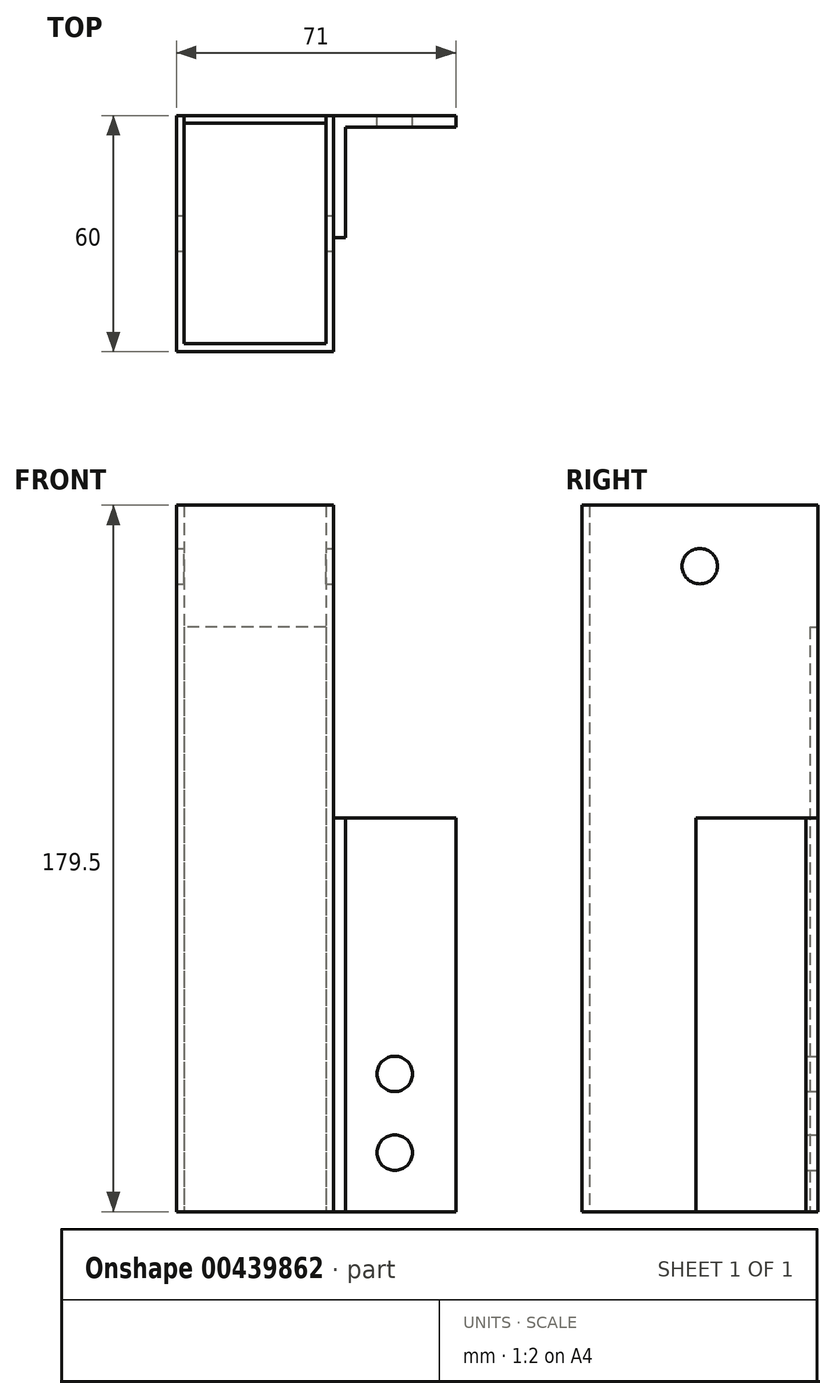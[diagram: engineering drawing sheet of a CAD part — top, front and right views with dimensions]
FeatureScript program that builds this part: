
annotation { "Feature Type Name" : "Feature", "Feature Type Description" : "" }
export const myFeature = defineFeature(function(context is Context, id is Id, definition is map)
    precondition{}
    {
        {
            assignVariable(context, id + "F0", {"name" : "x1", "anyValue" : 2});
        }
        {
            assignVariable(context, id + "F1", {"name" : "x3", "anyValue" : 31});
        }
        {
            assignVariable(context, id + "F2", {"name" : "x6", "anyValue" : 3});
        }
        {
            var Q0;
            Q0=qCreatedBy(makeId("Top.planeOp"),FACE);
            var sketch = newSketch(context, id + "F3", { "sketchPlane" : qUnion([Q0])});
            skLineSegment(sketch, "E0.bottom", {"start": v(0, 0) * mm, "end": v(-40, 0) * mm});
            skLineSegment(sketch, "E0.top", {"start": v(0, -60) * mm, "end": v(-40, -60) * mm});
            skLineSegment(sketch, "E0.left", {"start": v(0, 0) * mm, "end": v(0, -60) * mm});
            skLineSegment(sketch, "E0.right", {"start": v(-40, 0) * mm, "end": v(-40, -60) * mm});
            skLineSegment(sketch, "E1.bottom", {"start": v(0, 0) * mm, "end": v(31, 0) * mm});
            skLineSegment(sketch, "E1.top", {"start": v(0, -31) * mm, "end": v(31, -31) * mm});
            skLineSegment(sketch, "E1.left", {"start": v(0, 0) * mm, "end": v(0, -31) * mm});
            skLineSegment(sketch, "E1.right", {"start": v(31, 0) * mm, "end": v(31, -31) * mm});
            skSolve(sketch);
        }
        {
            var Q0;
            Q0=makeQuery(id+"F3.imprint","IMPRINT",FACE,{"disambiguationData":[TD([[makeQuery(id+"F3.imprint","IMPRINT",EDGE,{"derivedFrom":sQuery(id+"F3.wireOp",EDGE,"E0.bottom")}),1.0]])]});
            extrude(context, id + "F4", {"entities" : qUnion([Q0]), "depth" : (117.5 + (2 * getVariable(context, 'x3'))) * mm});
        }
        {
            var Q0;
            Q0=makeQuery(id+"F3.imprint","IMPRINT",FACE,{"disambiguationData":[TD([[makeQuery(id+"F3.imprint","IMPRINT",EDGE,{"derivedFrom":sQuery(id+"F3.wireOp",EDGE,"E1.bottom")}),-1.0]])]});
            extrude(context, id + "F5", {"entities" : qUnion([Q0]), "depth" : 100 * mm});
        }
        {
            var Q0;
            Q0=makeQuery(id+"F4.opExtrude","CAP_FACE",FACE,{"disambiguationData":[OSD([sQuery(id+"F3.wireOp",EDGE,"E0.bottom"),sQuery(id+"F3.wireOp",EDGE,"E0.top"),sQuery(id+"F3.wireOp",EDGE,"E0.left"),sQuery(id+"F3.wireOp",EDGE,"E0.right"),sQuery(id+"F3.wireOp",EDGE,"E1.left")])],"isStart":false});
            var Q1;
            Q1=makeQuery(id+"F4.opExtrude","CAP_FACE",FACE,{"disambiguationData":[OSD([sQuery(id+"F3.wireOp",EDGE,"E0.bottom"),sQuery(id+"F3.wireOp",EDGE,"E0.top"),sQuery(id+"F3.wireOp",EDGE,"E0.left"),sQuery(id+"F3.wireOp",EDGE,"E0.right"),sQuery(id+"F3.wireOp",EDGE,"E1.left")])],"isStart":true});
            shell(context, id + "F6", {"entities" : qUnion([Q0, Q1]), "thickness" : (getVariable(context, 'x1')) * mm});
        }
        {
            var Q0;
            Q0=makeQuery(id+"F5.opExtrude","CAP_FACE",FACE,{"disambiguationData":[OSD([sQuery(id+"F3.wireOp",EDGE,"E1.bottom"),sQuery(id+"F3.wireOp",EDGE,"E1.top"),sQuery(id+"F3.wireOp",EDGE,"E1.left"),sQuery(id+"F3.wireOp",EDGE,"E1.right")])],"isStart":false});
            var Q1;
            Q1=makeQuery(id+"F5.opExtrude","SWEPT_FACE",FACE,{"disambiguationData":[OSD([sQuery(id+"F3.wireOp",EDGE,"E1.top")])]});
            var Q2;
            Q2=makeQuery(id+"F5.opExtrude","SWEPT_FACE",FACE,{"disambiguationData":[OSD([sQuery(id+"F3.wireOp",EDGE,"E1.right")])]});
            var Q3;
            Q3=makeQuery(id+"F5.opExtrude","CAP_FACE",FACE,{"disambiguationData":[OSD([sQuery(id+"F3.wireOp",EDGE,"E1.bottom"),sQuery(id+"F3.wireOp",EDGE,"E1.top"),sQuery(id+"F3.wireOp",EDGE,"E1.left"),sQuery(id+"F3.wireOp",EDGE,"E1.right")])],"isStart":true});
            shell(context, id + "F7", {"entities" : qUnion([Q0, Q1, Q2, Q3]), "thickness" : (getVariable(context, 'x6')) * mm});
        }
        {
            var Q0;
            Q0=makeQuery(id+"F4.opExtrude","SWEPT_FACE",FACE,{"disambiguationData":[OSD([sQuery(id+"F3.wireOp",EDGE,"E0.bottom")])]});
            var sketch = newSketch(context, id + "F8", { "sketchPlane" : qUnion([Q0])});
            skLineSegment(sketch, "E2.bottom", {"start": v(2, 179.5) * mm, "end": v(38, 179.5) * mm});
            skLineSegment(sketch, "E2.top", {"start": v(2, 148.5) * mm, "end": v(38, 148.5) * mm});
            skLineSegment(sketch, "E2.left", {"start": v(2, 179.5) * mm, "end": v(2, 148.5) * mm});
            skLineSegment(sketch, "E2.right", {"start": v(38, 179.5) * mm, "end": v(38, 148.5) * mm});
            skSolve(sketch);
        }
        {
            var Q0;
            Q0=qSketchRegion(id+"F8",true);
            extrude(context, id + "F9", {"entities" : qUnion([Q0]), "operationType" : NewBodyOperationType.REMOVE, "endBound" : BoundingType.UP_TO_NEXT, "oppositeDirection" : true, "depth" : 25 * mm});
        }
        {
            var Q0;
            Q0=qCreatedBy(makeId("Front.planeOp"),FACE);
            var sketch = newSketch(context, id + "F10", { "sketchPlane" : qUnion([Q0])});
            skLineSegment(sketch, "E3.0.0", {"start": v(31, 0) * mm, "end": v(0, 0) * mm});
            skLineSegment(sketch, "E3.0.1", {"start": v(0, 0) * mm, "end": v(0, 100) * mm});
            skLineSegment(sketch, "E3.0.2", {"start": v(0, 100) * mm, "end": v(31, 100) * mm});
            skLineSegment(sketch, "E3.0.3", {"start": v(31, 100) * mm, "end": v(31, 0) * mm});
            skCircle(sketch, "E4", {"center": v(15.5, 15) * mm, "radius": 4.5 * mm});
            skCircle(sketch, "E5", {"center": v(15.5, 35) * mm, "radius": 4.5 * mm});
            skSolve(sketch);
        }
        {
            var Q0;
            Q0=makeQuery(id+"F10.imprint","IMPRINT",FACE,{"disambiguationData":[TD([[makeQuery(id+"F10.imprint","IMPRINT",EDGE,{"derivedFrom":sQuery(id+"F10.wireOp",EDGE,"E5")}),1.0]])]});
            var Q1;
            Q1=makeQuery(id+"F10.imprint","IMPRINT",FACE,{"disambiguationData":[TD([[makeQuery(id+"F10.imprint","IMPRINT",EDGE,{"derivedFrom":sQuery(id+"F10.wireOp",EDGE,"E4")}),1.0]])]});
            extrude(context, id + "F11", {"entities" : qUnion([Q0, Q1]), "operationType" : NewBodyOperationType.REMOVE, "endBound" : BoundingType.UP_TO_NEXT, "depth" : 25 * mm});
        }
        {
            var Q0;
            Q0=qCreatedBy(makeId("Right.planeOp"),FACE);
            var sketch = newSketch(context, id + "F12", { "sketchPlane" : qUnion([Q0])});
            skLineSegment(sketch, "E6.0.0", {"start": v(-60, 0) * mm, "end": v(0, 0) * mm});
            skLineSegment(sketch, "E6.0.1", {"start": v(0, 0) * mm, "end": v(0, 179.5) * mm});
            skLineSegment(sketch, "E6.0.2", {"start": v(0, 179.5) * mm, "end": v(-60, 179.5) * mm});
            skLineSegment(sketch, "E6.0.3", {"start": v(-60, 179.5) * mm, "end": v(-60, 0) * mm});
            skCircle(sketch, "E7", {"center": v(-30, 164) * mm, "radius": 4.5 * mm});
            skSolve(sketch);
        }
        {
            var Q0;
            Q0=makeQuery(id+"F12.imprint","IMPRINT",FACE,{"disambiguationData":[TD([[makeQuery(id+"F12.imprint","IMPRINT",EDGE,{"derivedFrom":sQuery(id+"F12.wireOp",EDGE,"E7")}),1.0]])]});
            extrude(context, id + "F13", {"entities" : qUnion([Q0]), "operationType" : NewBodyOperationType.REMOVE, "endBound" : BoundingType.THROUGH_ALL, "oppositeDirection" : true, "depth" : 25 * mm});
        }
    });
